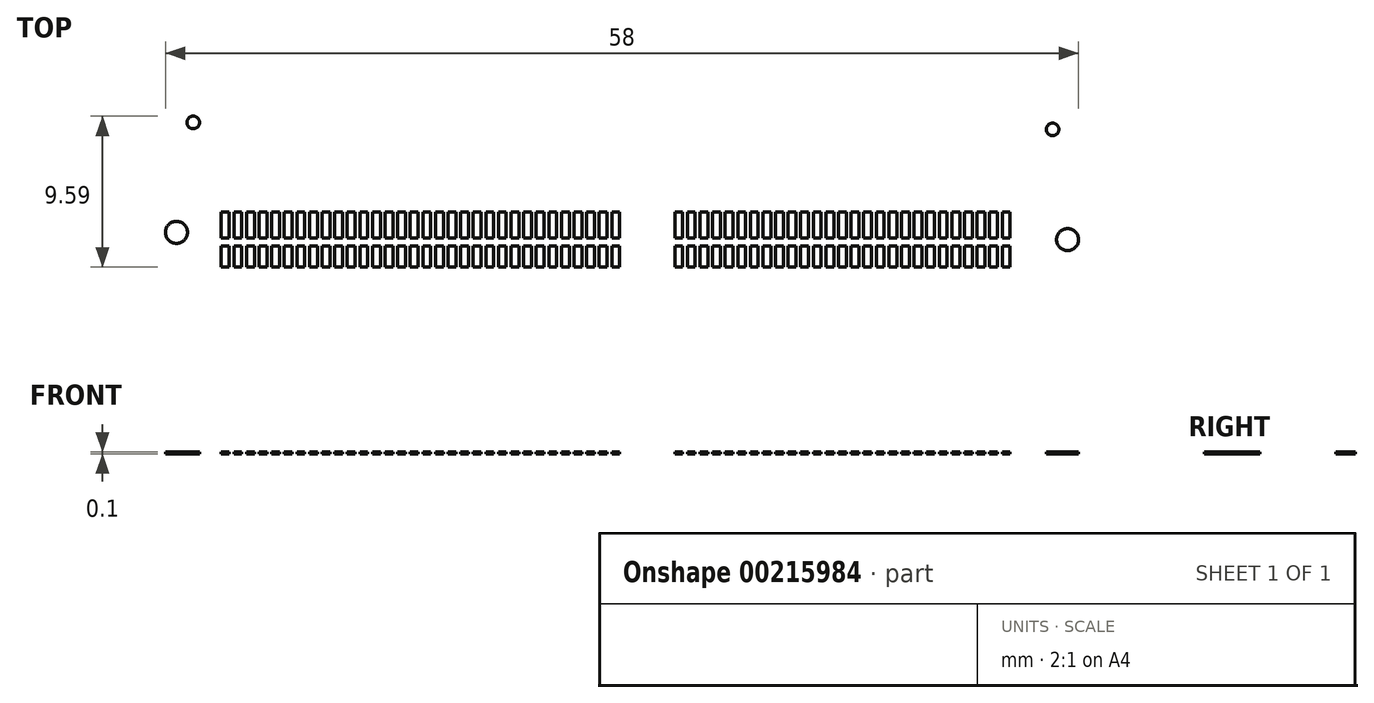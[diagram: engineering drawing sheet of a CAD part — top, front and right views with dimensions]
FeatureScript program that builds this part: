
annotation { "Feature Type Name" : "Feature", "Feature Type Description" : "" }
export const myFeature = defineFeature(function(context is Context, id is Id, definition is map)
    precondition{}
    {
        {
            var Q0;
            Q0=qCreatedBy(makeId("Top.planeOp"), FACE);
            var sketch = newSketch(context, id + "F0", { "sketchPlane" : qUnion([Q0])});
            skLineSegment(sketch, "E0.bottom", {"start": v(-25.45, 1.75) * mm, "end": v(-24.95, 1.75) * mm});
            skLineSegment(sketch, "E0.top", {"start": v(-25.45, 0.1) * mm, "end": v(-24.95, 0.1) * mm});
            skLineSegment(sketch, "E0.left", {"start": v(-25.45, 1.75) * mm, "end": v(-25.45, 0.1) * mm});
            skLineSegment(sketch, "E0.right", {"start": v(-24.95, 1.75) * mm, "end": v(-24.95, 0.1) * mm});
            skLineSegment(sketch, "E1.bottom", {"start": v(-25.45, -0.4) * mm, "end": v(-24.95, -0.4) * mm});
            skLineSegment(sketch, "E1.top", {"start": v(-25.45, -1.75) * mm, "end": v(-24.95, -1.75) * mm});
            skLineSegment(sketch, "E1.left", {"start": v(-25.45, -0.4) * mm, "end": v(-25.45, -1.75) * mm});
            skLineSegment(sketch, "E1.right", {"start": v(-24.95, -0.4) * mm, "end": v(-24.95, -1.75) * mm});
            skPoint(sketch, "E2", {"position": v(-25.2, -1.75) * mm});
            skLineSegment(sketch, "E3.1.0.0", {"start": v(-24.15, 1.75) * mm, "end": v(-24.15, 0.1) * mm});
            skLineSegment(sketch, "E3.1.0.1", {"start": v(-24.65, -0.4) * mm, "end": v(-24.65, -1.75) * mm});
            skLineSegment(sketch, "E3.1.0.2", {"start": v(-24.65, 0.1) * mm, "end": v(-24.15, 0.1) * mm});
            skLineSegment(sketch, "E3.1.0.3", {"start": v(-24.15, -0.4) * mm, "end": v(-24.15, -1.75) * mm});
            skPoint(sketch, "E3.1.0.4", {"position": v(-24.4, -1.75) * mm});
            skLineSegment(sketch, "E3.1.0.5", {"start": v(-24.65, -0.4) * mm, "end": v(-24.15, -0.4) * mm});
            skLineSegment(sketch, "E3.1.0.6", {"start": v(-24.65, 1.75) * mm, "end": v(-24.15, 1.75) * mm});
            skLineSegment(sketch, "E3.1.0.7", {"start": v(-24.65, 1.75) * mm, "end": v(-24.65, 0.1) * mm});
            skLineSegment(sketch, "E3.1.0.8", {"start": v(-24.65, -1.75) * mm, "end": v(-24.15, -1.75) * mm});
            skLineSegment(sketch, "E3.2.0.0", {"start": v(-23.35, 1.75) * mm, "end": v(-23.35, 0.1) * mm});
            skLineSegment(sketch, "E3.2.0.1", {"start": v(-23.85, -0.4) * mm, "end": v(-23.85, -1.75) * mm});
            skLineSegment(sketch, "E3.2.0.2", {"start": v(-23.85, 0.1) * mm, "end": v(-23.35, 0.1) * mm});
            skLineSegment(sketch, "E3.2.0.3", {"start": v(-23.35, -0.4) * mm, "end": v(-23.35, -1.75) * mm});
            skPoint(sketch, "E3.2.0.4", {"position": v(-23.6, -1.75) * mm});
            skLineSegment(sketch, "E3.2.0.5", {"start": v(-23.85, -0.4) * mm, "end": v(-23.35, -0.4) * mm});
            skLineSegment(sketch, "E3.2.0.6", {"start": v(-23.85, 1.75) * mm, "end": v(-23.35, 1.75) * mm});
            skLineSegment(sketch, "E3.2.0.7", {"start": v(-23.85, 1.75) * mm, "end": v(-23.85, 0.1) * mm});
            skLineSegment(sketch, "E3.2.0.8", {"start": v(-23.85, -1.75) * mm, "end": v(-23.35, -1.75) * mm});
            skLineSegment(sketch, "E3.3.0.0", {"start": v(-22.55, 1.75) * mm, "end": v(-22.55, 0.1) * mm});
            skLineSegment(sketch, "E3.3.0.1", {"start": v(-23.05, -0.4) * mm, "end": v(-23.05, -1.75) * mm});
            skLineSegment(sketch, "E3.3.0.2", {"start": v(-23.05, 0.1) * mm, "end": v(-22.55, 0.1) * mm});
            skLineSegment(sketch, "E3.3.0.3", {"start": v(-22.55, -0.4) * mm, "end": v(-22.55, -1.75) * mm});
            skPoint(sketch, "E3.3.0.4", {"position": v(-22.8, -1.75) * mm});
            skLineSegment(sketch, "E3.3.0.5", {"start": v(-23.05, -0.4) * mm, "end": v(-22.55, -0.4) * mm});
            skLineSegment(sketch, "E3.3.0.6", {"start": v(-23.05, 1.75) * mm, "end": v(-22.55, 1.75) * mm});
            skLineSegment(sketch, "E3.3.0.7", {"start": v(-23.05, 1.75) * mm, "end": v(-23.05, 0.1) * mm});
            skLineSegment(sketch, "E3.3.0.8", {"start": v(-23.05, -1.75) * mm, "end": v(-22.55, -1.75) * mm});
            skLineSegment(sketch, "E3.4.0.0", {"start": v(-21.75, 1.75) * mm, "end": v(-21.75, 0.1) * mm});
            skLineSegment(sketch, "E3.4.0.1", {"start": v(-22.25, -0.4) * mm, "end": v(-22.25, -1.75) * mm});
            skLineSegment(sketch, "E3.4.0.2", {"start": v(-22.25, 0.1) * mm, "end": v(-21.75, 0.1) * mm});
            skLineSegment(sketch, "E3.4.0.3", {"start": v(-21.75, -0.4) * mm, "end": v(-21.75, -1.75) * mm});
            skPoint(sketch, "E3.4.0.4", {"position": v(-22, -1.75) * mm});
            skLineSegment(sketch, "E3.4.0.5", {"start": v(-22.25, -0.4) * mm, "end": v(-21.75, -0.4) * mm});
            skLineSegment(sketch, "E3.4.0.6", {"start": v(-22.25, 1.75) * mm, "end": v(-21.75, 1.75) * mm});
            skLineSegment(sketch, "E3.4.0.7", {"start": v(-22.25, 1.75) * mm, "end": v(-22.25, 0.1) * mm});
            skLineSegment(sketch, "E3.4.0.8", {"start": v(-22.25, -1.75) * mm, "end": v(-21.75, -1.75) * mm});
            skLineSegment(sketch, "E3.5.0.0", {"start": v(-20.95, 1.75) * mm, "end": v(-20.95, 0.1) * mm});
            skLineSegment(sketch, "E3.5.0.1", {"start": v(-21.45, -0.4) * mm, "end": v(-21.45, -1.75) * mm});
            skLineSegment(sketch, "E3.5.0.2", {"start": v(-21.45, 0.1) * mm, "end": v(-20.95, 0.1) * mm});
            skLineSegment(sketch, "E3.5.0.3", {"start": v(-20.95, -0.4) * mm, "end": v(-20.95, -1.75) * mm});
            skPoint(sketch, "E3.5.0.4", {"position": v(-21.2, -1.75) * mm});
            skLineSegment(sketch, "E3.5.0.5", {"start": v(-21.45, -0.4) * mm, "end": v(-20.95, -0.4) * mm});
            skLineSegment(sketch, "E3.5.0.6", {"start": v(-21.45, 1.75) * mm, "end": v(-20.95, 1.75) * mm});
            skLineSegment(sketch, "E3.5.0.7", {"start": v(-21.45, 1.75) * mm, "end": v(-21.45, 0.1) * mm});
            skLineSegment(sketch, "E3.5.0.8", {"start": v(-21.45, -1.75) * mm, "end": v(-20.95, -1.75) * mm});
            skLineSegment(sketch, "E3.6.0.0", {"start": v(-20.15, 1.75) * mm, "end": v(-20.15, 0.1) * mm});
            skLineSegment(sketch, "E3.6.0.1", {"start": v(-20.65, -0.4) * mm, "end": v(-20.65, -1.75) * mm});
            skLineSegment(sketch, "E3.6.0.2", {"start": v(-20.65, 0.1) * mm, "end": v(-20.15, 0.1) * mm});
            skLineSegment(sketch, "E3.6.0.3", {"start": v(-20.15, -0.4) * mm, "end": v(-20.15, -1.75) * mm});
            skPoint(sketch, "E3.6.0.4", {"position": v(-20.4, -1.75) * mm});
            skLineSegment(sketch, "E3.6.0.5", {"start": v(-20.65, -0.4) * mm, "end": v(-20.15, -0.4) * mm});
            skLineSegment(sketch, "E3.6.0.6", {"start": v(-20.65, 1.75) * mm, "end": v(-20.15, 1.75) * mm});
            skLineSegment(sketch, "E3.6.0.7", {"start": v(-20.65, 1.75) * mm, "end": v(-20.65, 0.1) * mm});
            skLineSegment(sketch, "E3.6.0.8", {"start": v(-20.65, -1.75) * mm, "end": v(-20.15, -1.75) * mm});
            skLineSegment(sketch, "E3.7.0.0", {"start": v(-19.35, 1.75) * mm, "end": v(-19.35, 0.1) * mm});
            skLineSegment(sketch, "E3.7.0.1", {"start": v(-19.85, -0.4) * mm, "end": v(-19.85, -1.75) * mm});
            skLineSegment(sketch, "E3.7.0.2", {"start": v(-19.85, 0.1) * mm, "end": v(-19.35, 0.1) * mm});
            skLineSegment(sketch, "E3.7.0.3", {"start": v(-19.35, -0.4) * mm, "end": v(-19.35, -1.75) * mm});
            skPoint(sketch, "E3.7.0.4", {"position": v(-19.6, -1.75) * mm});
            skLineSegment(sketch, "E3.7.0.5", {"start": v(-19.85, -0.4) * mm, "end": v(-19.35, -0.4) * mm});
            skLineSegment(sketch, "E3.7.0.6", {"start": v(-19.85, 1.75) * mm, "end": v(-19.35, 1.75) * mm});
            skLineSegment(sketch, "E3.7.0.7", {"start": v(-19.85, 1.75) * mm, "end": v(-19.85, 0.1) * mm});
            skLineSegment(sketch, "E3.7.0.8", {"start": v(-19.85, -1.75) * mm, "end": v(-19.35, -1.75) * mm});
            skLineSegment(sketch, "E3.8.0.0", {"start": v(-18.55, 1.75) * mm, "end": v(-18.55, 0.1) * mm});
            skLineSegment(sketch, "E3.8.0.1", {"start": v(-19.05, -0.4) * mm, "end": v(-19.05, -1.75) * mm});
            skLineSegment(sketch, "E3.8.0.2", {"start": v(-19.05, 0.1) * mm, "end": v(-18.55, 0.1) * mm});
            skLineSegment(sketch, "E3.8.0.3", {"start": v(-18.55, -0.4) * mm, "end": v(-18.55, -1.75) * mm});
            skPoint(sketch, "E3.8.0.4", {"position": v(-18.8, -1.75) * mm});
            skLineSegment(sketch, "E3.8.0.5", {"start": v(-19.05, -0.4) * mm, "end": v(-18.55, -0.4) * mm});
            skLineSegment(sketch, "E3.8.0.6", {"start": v(-19.05, 1.75) * mm, "end": v(-18.55, 1.75) * mm});
            skLineSegment(sketch, "E3.8.0.7", {"start": v(-19.05, 1.75) * mm, "end": v(-19.05, 0.1) * mm});
            skLineSegment(sketch, "E3.8.0.8", {"start": v(-19.05, -1.75) * mm, "end": v(-18.55, -1.75) * mm});
            skLineSegment(sketch, "E3.9.0.0", {"start": v(-17.75, 1.75) * mm, "end": v(-17.75, 0.1) * mm});
            skLineSegment(sketch, "E3.9.0.1", {"start": v(-18.25, -0.4) * mm, "end": v(-18.25, -1.75) * mm});
            skLineSegment(sketch, "E3.9.0.2", {"start": v(-18.25, 0.1) * mm, "end": v(-17.75, 0.1) * mm});
            skLineSegment(sketch, "E3.9.0.3", {"start": v(-17.75, -0.4) * mm, "end": v(-17.75, -1.75) * mm});
            skPoint(sketch, "E3.9.0.4", {"position": v(-18, -1.75) * mm});
            skLineSegment(sketch, "E3.9.0.5", {"start": v(-18.25, -0.4) * mm, "end": v(-17.75, -0.4) * mm});
            skLineSegment(sketch, "E3.9.0.6", {"start": v(-18.25, 1.75) * mm, "end": v(-17.75, 1.75) * mm});
            skLineSegment(sketch, "E3.9.0.7", {"start": v(-18.25, 1.75) * mm, "end": v(-18.25, 0.1) * mm});
            skLineSegment(sketch, "E3.9.0.8", {"start": v(-18.25, -1.75) * mm, "end": v(-17.75, -1.75) * mm});
            skLineSegment(sketch, "E3.10.0.0", {"start": v(-16.95, 1.75) * mm, "end": v(-16.95, 0.1) * mm});
            skLineSegment(sketch, "E3.10.0.1", {"start": v(-17.45, -0.4) * mm, "end": v(-17.45, -1.75) * mm});
            skLineSegment(sketch, "E3.10.0.2", {"start": v(-17.45, 0.1) * mm, "end": v(-16.95, 0.1) * mm});
            skLineSegment(sketch, "E3.10.0.3", {"start": v(-16.95, -0.4) * mm, "end": v(-16.95, -1.75) * mm});
            skPoint(sketch, "E3.10.0.4", {"position": v(-17.2, -1.75) * mm});
            skLineSegment(sketch, "E3.10.0.5", {"start": v(-17.45, -0.4) * mm, "end": v(-16.95, -0.4) * mm});
            skLineSegment(sketch, "E3.10.0.6", {"start": v(-17.45, 1.75) * mm, "end": v(-16.95, 1.75) * mm});
            skLineSegment(sketch, "E3.10.0.7", {"start": v(-17.45, 1.75) * mm, "end": v(-17.45, 0.1) * mm});
            skLineSegment(sketch, "E3.10.0.8", {"start": v(-17.45, -1.75) * mm, "end": v(-16.95, -1.75) * mm});
            skLineSegment(sketch, "E3.11.0.0", {"start": v(-16.15, 1.75) * mm, "end": v(-16.15, 0.1) * mm});
            skLineSegment(sketch, "E3.11.0.1", {"start": v(-16.65, -0.4) * mm, "end": v(-16.65, -1.75) * mm});
            skLineSegment(sketch, "E3.11.0.2", {"start": v(-16.65, 0.1) * mm, "end": v(-16.15, 0.1) * mm});
            skLineSegment(sketch, "E3.11.0.3", {"start": v(-16.15, -0.4) * mm, "end": v(-16.15, -1.75) * mm});
            skPoint(sketch, "E3.11.0.4", {"position": v(-16.4, -1.75) * mm});
            skLineSegment(sketch, "E3.11.0.5", {"start": v(-16.65, -0.4) * mm, "end": v(-16.15, -0.4) * mm});
            skLineSegment(sketch, "E3.11.0.6", {"start": v(-16.65, 1.75) * mm, "end": v(-16.15, 1.75) * mm});
            skLineSegment(sketch, "E3.11.0.7", {"start": v(-16.65, 1.75) * mm, "end": v(-16.65, 0.1) * mm});
            skLineSegment(sketch, "E3.11.0.8", {"start": v(-16.65, -1.75) * mm, "end": v(-16.15, -1.75) * mm});
            skLineSegment(sketch, "E3.12.0.0", {"start": v(-15.35, 1.75) * mm, "end": v(-15.35, 0.1) * mm});
            skLineSegment(sketch, "E3.12.0.1", {"start": v(-15.85, -0.4) * mm, "end": v(-15.85, -1.75) * mm});
            skLineSegment(sketch, "E3.12.0.2", {"start": v(-15.85, 0.1) * mm, "end": v(-15.35, 0.1) * mm});
            skLineSegment(sketch, "E3.12.0.3", {"start": v(-15.35, -0.4) * mm, "end": v(-15.35, -1.75) * mm});
            skPoint(sketch, "E3.12.0.4", {"position": v(-15.6, -1.75) * mm});
            skLineSegment(sketch, "E3.12.0.5", {"start": v(-15.85, -0.4) * mm, "end": v(-15.35, -0.4) * mm});
            skLineSegment(sketch, "E3.12.0.6", {"start": v(-15.85, 1.75) * mm, "end": v(-15.35, 1.75) * mm});
            skLineSegment(sketch, "E3.12.0.7", {"start": v(-15.85, 1.75) * mm, "end": v(-15.85, 0.1) * mm});
            skLineSegment(sketch, "E3.12.0.8", {"start": v(-15.85, -1.75) * mm, "end": v(-15.35, -1.75) * mm});
            skLineSegment(sketch, "E3.13.0.0", {"start": v(-14.55, 1.75) * mm, "end": v(-14.55, 0.1) * mm});
            skLineSegment(sketch, "E3.13.0.1", {"start": v(-15.05, -0.4) * mm, "end": v(-15.05, -1.75) * mm});
            skLineSegment(sketch, "E3.13.0.2", {"start": v(-15.05, 0.1) * mm, "end": v(-14.55, 0.1) * mm});
            skLineSegment(sketch, "E3.13.0.3", {"start": v(-14.55, -0.4) * mm, "end": v(-14.55, -1.75) * mm});
            skPoint(sketch, "E3.13.0.4", {"position": v(-14.8, -1.75) * mm});
            skLineSegment(sketch, "E3.13.0.5", {"start": v(-15.05, -0.4) * mm, "end": v(-14.55, -0.4) * mm});
            skLineSegment(sketch, "E3.13.0.6", {"start": v(-15.05, 1.75) * mm, "end": v(-14.55, 1.75) * mm});
            skLineSegment(sketch, "E3.13.0.7", {"start": v(-15.05, 1.75) * mm, "end": v(-15.05, 0.1) * mm});
            skLineSegment(sketch, "E3.13.0.8", {"start": v(-15.05, -1.75) * mm, "end": v(-14.55, -1.75) * mm});
            skLineSegment(sketch, "E3.14.0.0", {"start": v(-13.75, 1.75) * mm, "end": v(-13.75, 0.1) * mm});
            skLineSegment(sketch, "E3.14.0.1", {"start": v(-14.25, -0.4) * mm, "end": v(-14.25, -1.75) * mm});
            skLineSegment(sketch, "E3.14.0.2", {"start": v(-14.25, 0.1) * mm, "end": v(-13.75, 0.1) * mm});
            skLineSegment(sketch, "E3.14.0.3", {"start": v(-13.75, -0.4) * mm, "end": v(-13.75, -1.75) * mm});
            skPoint(sketch, "E3.14.0.4", {"position": v(-14, -1.75) * mm});
            skLineSegment(sketch, "E3.14.0.5", {"start": v(-14.25, -0.4) * mm, "end": v(-13.75, -0.4) * mm});
            skLineSegment(sketch, "E3.14.0.6", {"start": v(-14.25, 1.75) * mm, "end": v(-13.75, 1.75) * mm});
            skLineSegment(sketch, "E3.14.0.7", {"start": v(-14.25, 1.75) * mm, "end": v(-14.25, 0.1) * mm});
            skLineSegment(sketch, "E3.14.0.8", {"start": v(-14.25, -1.75) * mm, "end": v(-13.75, -1.75) * mm});
            skLineSegment(sketch, "E3.15.0.0", {"start": v(-12.95, 1.75) * mm, "end": v(-12.95, 0.1) * mm});
            skLineSegment(sketch, "E3.15.0.1", {"start": v(-13.45, -0.4) * mm, "end": v(-13.45, -1.75) * mm});
            skLineSegment(sketch, "E3.15.0.2", {"start": v(-13.45, 0.1) * mm, "end": v(-12.95, 0.1) * mm});
            skLineSegment(sketch, "E3.15.0.3", {"start": v(-12.95, -0.4) * mm, "end": v(-12.95, -1.75) * mm});
            skPoint(sketch, "E3.15.0.4", {"position": v(-13.2, -1.75) * mm});
            skLineSegment(sketch, "E3.15.0.5", {"start": v(-13.45, -0.4) * mm, "end": v(-12.95, -0.4) * mm});
            skLineSegment(sketch, "E3.15.0.6", {"start": v(-13.45, 1.75) * mm, "end": v(-12.95, 1.75) * mm});
            skLineSegment(sketch, "E3.15.0.7", {"start": v(-13.45, 1.75) * mm, "end": v(-13.45, 0.1) * mm});
            skLineSegment(sketch, "E3.15.0.8", {"start": v(-13.45, -1.75) * mm, "end": v(-12.95, -1.75) * mm});
            skLineSegment(sketch, "E3.16.0.0", {"start": v(-12.15, 1.75) * mm, "end": v(-12.15, 0.1) * mm});
            skLineSegment(sketch, "E3.16.0.1", {"start": v(-12.65, -0.4) * mm, "end": v(-12.65, -1.75) * mm});
            skLineSegment(sketch, "E3.16.0.2", {"start": v(-12.65, 0.1) * mm, "end": v(-12.15, 0.1) * mm});
            skLineSegment(sketch, "E3.16.0.3", {"start": v(-12.15, -0.4) * mm, "end": v(-12.15, -1.75) * mm});
            skPoint(sketch, "E3.16.0.4", {"position": v(-12.4, -1.75) * mm});
            skLineSegment(sketch, "E3.16.0.5", {"start": v(-12.65, -0.4) * mm, "end": v(-12.15, -0.4) * mm});
            skLineSegment(sketch, "E3.16.0.6", {"start": v(-12.65, 1.75) * mm, "end": v(-12.15, 1.75) * mm});
            skLineSegment(sketch, "E3.16.0.7", {"start": v(-12.65, 1.75) * mm, "end": v(-12.65, 0.1) * mm});
            skLineSegment(sketch, "E3.16.0.8", {"start": v(-12.65, -1.75) * mm, "end": v(-12.15, -1.75) * mm});
            skLineSegment(sketch, "E3.17.0.0", {"start": v(-11.35, 1.75) * mm, "end": v(-11.35, 0.1) * mm});
            skLineSegment(sketch, "E3.17.0.1", {"start": v(-11.85, -0.4) * mm, "end": v(-11.85, -1.75) * mm});
            skLineSegment(sketch, "E3.17.0.2", {"start": v(-11.85, 0.1) * mm, "end": v(-11.35, 0.1) * mm});
            skLineSegment(sketch, "E3.17.0.3", {"start": v(-11.35, -0.4) * mm, "end": v(-11.35, -1.75) * mm});
            skPoint(sketch, "E3.17.0.4", {"position": v(-11.6, -1.75) * mm});
            skLineSegment(sketch, "E3.17.0.5", {"start": v(-11.85, -0.4) * mm, "end": v(-11.35, -0.4) * mm});
            skLineSegment(sketch, "E3.17.0.6", {"start": v(-11.85, 1.75) * mm, "end": v(-11.35, 1.75) * mm});
            skLineSegment(sketch, "E3.17.0.7", {"start": v(-11.85, 1.75) * mm, "end": v(-11.85, 0.1) * mm});
            skLineSegment(sketch, "E3.17.0.8", {"start": v(-11.85, -1.75) * mm, "end": v(-11.35, -1.75) * mm});
            skLineSegment(sketch, "E3.18.0.0", {"start": v(-10.55, 1.75) * mm, "end": v(-10.55, 0.1) * mm});
            skLineSegment(sketch, "E3.18.0.1", {"start": v(-11.05, -0.4) * mm, "end": v(-11.05, -1.75) * mm});
            skLineSegment(sketch, "E3.18.0.2", {"start": v(-11.05, 0.1) * mm, "end": v(-10.55, 0.1) * mm});
            skLineSegment(sketch, "E3.18.0.3", {"start": v(-10.55, -0.4) * mm, "end": v(-10.55, -1.75) * mm});
            skPoint(sketch, "E3.18.0.4", {"position": v(-10.8, -1.75) * mm});
            skLineSegment(sketch, "E3.18.0.5", {"start": v(-11.05, -0.4) * mm, "end": v(-10.55, -0.4) * mm});
            skLineSegment(sketch, "E3.18.0.6", {"start": v(-11.05, 1.75) * mm, "end": v(-10.55, 1.75) * mm});
            skLineSegment(sketch, "E3.18.0.7", {"start": v(-11.05, 1.75) * mm, "end": v(-11.05, 0.1) * mm});
            skLineSegment(sketch, "E3.18.0.8", {"start": v(-11.05, -1.75) * mm, "end": v(-10.55, -1.75) * mm});
            skLineSegment(sketch, "E3.19.0.0", {"start": v(-9.75, 1.75) * mm, "end": v(-9.75, 0.1) * mm});
            skLineSegment(sketch, "E3.19.0.1", {"start": v(-10.25, -0.4) * mm, "end": v(-10.25, -1.75) * mm});
            skLineSegment(sketch, "E3.19.0.2", {"start": v(-10.25, 0.1) * mm, "end": v(-9.75, 0.1) * mm});
            skLineSegment(sketch, "E3.19.0.3", {"start": v(-9.75, -0.4) * mm, "end": v(-9.75, -1.75) * mm});
            skPoint(sketch, "E3.19.0.4", {"position": v(-10, -1.75) * mm});
            skLineSegment(sketch, "E3.19.0.5", {"start": v(-10.25, -0.4) * mm, "end": v(-9.75, -0.4) * mm});
            skLineSegment(sketch, "E3.19.0.6", {"start": v(-10.25, 1.75) * mm, "end": v(-9.75, 1.75) * mm});
            skLineSegment(sketch, "E3.19.0.7", {"start": v(-10.25, 1.75) * mm, "end": v(-10.25, 0.1) * mm});
            skLineSegment(sketch, "E3.19.0.8", {"start": v(-10.25, -1.75) * mm, "end": v(-9.75, -1.75) * mm});
            skLineSegment(sketch, "E3.20.0.0", {"start": v(-8.95, 1.75) * mm, "end": v(-8.95, 0.1) * mm});
            skLineSegment(sketch, "E3.20.0.1", {"start": v(-9.45, -0.4) * mm, "end": v(-9.45, -1.75) * mm});
            skLineSegment(sketch, "E3.20.0.2", {"start": v(-9.45, 0.1) * mm, "end": v(-8.95, 0.1) * mm});
            skLineSegment(sketch, "E3.20.0.3", {"start": v(-8.95, -0.4) * mm, "end": v(-8.95, -1.75) * mm});
            skPoint(sketch, "E3.20.0.4", {"position": v(-9.2, -1.75) * mm});
            skLineSegment(sketch, "E3.20.0.5", {"start": v(-9.45, -0.4) * mm, "end": v(-8.95, -0.4) * mm});
            skLineSegment(sketch, "E3.20.0.6", {"start": v(-9.45, 1.75) * mm, "end": v(-8.95, 1.75) * mm});
            skLineSegment(sketch, "E3.20.0.7", {"start": v(-9.45, 1.75) * mm, "end": v(-9.45, 0.1) * mm});
            skLineSegment(sketch, "E3.20.0.8", {"start": v(-9.45, -1.75) * mm, "end": v(-8.95, -1.75) * mm});
            skLineSegment(sketch, "E3.21.0.0", {"start": v(-8.15, 1.75) * mm, "end": v(-8.15, 0.1) * mm});
            skLineSegment(sketch, "E3.21.0.1", {"start": v(-8.65, -0.4) * mm, "end": v(-8.65, -1.75) * mm});
            skLineSegment(sketch, "E3.21.0.2", {"start": v(-8.65, 0.1) * mm, "end": v(-8.15, 0.1) * mm});
            skLineSegment(sketch, "E3.21.0.3", {"start": v(-8.15, -0.4) * mm, "end": v(-8.15, -1.75) * mm});
            skPoint(sketch, "E3.21.0.4", {"position": v(-8.4, -1.75) * mm});
            skLineSegment(sketch, "E3.21.0.5", {"start": v(-8.65, -0.4) * mm, "end": v(-8.15, -0.4) * mm});
            skLineSegment(sketch, "E3.21.0.6", {"start": v(-8.65, 1.75) * mm, "end": v(-8.15, 1.75) * mm});
            skLineSegment(sketch, "E3.21.0.7", {"start": v(-8.65, 1.75) * mm, "end": v(-8.65, 0.1) * mm});
            skLineSegment(sketch, "E3.21.0.8", {"start": v(-8.65, -1.75) * mm, "end": v(-8.15, -1.75) * mm});
            skLineSegment(sketch, "E3.22.0.0", {"start": v(-7.35, 1.75) * mm, "end": v(-7.35, 0.1) * mm});
            skLineSegment(sketch, "E3.22.0.1", {"start": v(-7.85, -0.4) * mm, "end": v(-7.85, -1.75) * mm});
            skLineSegment(sketch, "E3.22.0.2", {"start": v(-7.85, 0.1) * mm, "end": v(-7.35, 0.1) * mm});
            skLineSegment(sketch, "E3.22.0.3", {"start": v(-7.35, -0.4) * mm, "end": v(-7.35, -1.75) * mm});
            skPoint(sketch, "E3.22.0.4", {"position": v(-7.6, -1.75) * mm});
            skLineSegment(sketch, "E3.22.0.5", {"start": v(-7.85, -0.4) * mm, "end": v(-7.35, -0.4) * mm});
            skLineSegment(sketch, "E3.22.0.6", {"start": v(-7.85, 1.75) * mm, "end": v(-7.35, 1.75) * mm});
            skLineSegment(sketch, "E3.22.0.7", {"start": v(-7.85, 1.75) * mm, "end": v(-7.85, 0.1) * mm});
            skLineSegment(sketch, "E3.22.0.8", {"start": v(-7.85, -1.75) * mm, "end": v(-7.35, -1.75) * mm});
            skLineSegment(sketch, "E3.23.0.0", {"start": v(-6.55, 1.75) * mm, "end": v(-6.55, 0.1) * mm});
            skLineSegment(sketch, "E3.23.0.1", {"start": v(-7.05, -0.4) * mm, "end": v(-7.05, -1.75) * mm});
            skLineSegment(sketch, "E3.23.0.2", {"start": v(-7.05, 0.1) * mm, "end": v(-6.55, 0.1) * mm});
            skLineSegment(sketch, "E3.23.0.3", {"start": v(-6.55, -0.4) * mm, "end": v(-6.55, -1.75) * mm});
            skPoint(sketch, "E3.23.0.4", {"position": v(-6.8, -1.75) * mm});
            skLineSegment(sketch, "E3.23.0.5", {"start": v(-7.05, -0.4) * mm, "end": v(-6.55, -0.4) * mm});
            skLineSegment(sketch, "E3.23.0.6", {"start": v(-7.05, 1.75) * mm, "end": v(-6.55, 1.75) * mm});
            skLineSegment(sketch, "E3.23.0.7", {"start": v(-7.05, 1.75) * mm, "end": v(-7.05, 0.1) * mm});
            skLineSegment(sketch, "E3.23.0.8", {"start": v(-7.05, -1.75) * mm, "end": v(-6.55, -1.75) * mm});
            skLineSegment(sketch, "E3.24.0.0", {"start": v(-5.75, 1.75) * mm, "end": v(-5.75, 0.1) * mm});
            skLineSegment(sketch, "E3.24.0.1", {"start": v(-6.25, -0.4) * mm, "end": v(-6.25, -1.75) * mm});
            skLineSegment(sketch, "E3.24.0.2", {"start": v(-6.25, 0.1) * mm, "end": v(-5.75, 0.1) * mm});
            skLineSegment(sketch, "E3.24.0.3", {"start": v(-5.75, -0.4) * mm, "end": v(-5.75, -1.75) * mm});
            skPoint(sketch, "E3.24.0.4", {"position": v(-6, -1.75) * mm});
            skLineSegment(sketch, "E3.24.0.5", {"start": v(-6.25, -0.4) * mm, "end": v(-5.75, -0.4) * mm});
            skLineSegment(sketch, "E3.24.0.6", {"start": v(-6.25, 1.75) * mm, "end": v(-5.75, 1.75) * mm});
            skLineSegment(sketch, "E3.24.0.7", {"start": v(-6.25, 1.75) * mm, "end": v(-6.25, 0.1) * mm});
            skLineSegment(sketch, "E3.24.0.8", {"start": v(-6.25, -1.75) * mm, "end": v(-5.75, -1.75) * mm});
            skLineSegment(sketch, "E3.25.0.0", {"start": v(-4.95, 1.75) * mm, "end": v(-4.95, 0.1) * mm});
            skLineSegment(sketch, "E3.25.0.1", {"start": v(-5.45, -0.4) * mm, "end": v(-5.45, -1.75) * mm});
            skLineSegment(sketch, "E3.25.0.2", {"start": v(-5.45, 0.1) * mm, "end": v(-4.95, 0.1) * mm});
            skLineSegment(sketch, "E3.25.0.3", {"start": v(-4.95, -0.4) * mm, "end": v(-4.95, -1.75) * mm});
            skPoint(sketch, "E3.25.0.4", {"position": v(-5.2, -1.75) * mm});
            skLineSegment(sketch, "E3.25.0.5", {"start": v(-5.45, -0.4) * mm, "end": v(-4.95, -0.4) * mm});
            skLineSegment(sketch, "E3.25.0.6", {"start": v(-5.45, 1.75) * mm, "end": v(-4.95, 1.75) * mm});
            skLineSegment(sketch, "E3.25.0.7", {"start": v(-5.45, 1.75) * mm, "end": v(-5.45, 0.1) * mm});
            skLineSegment(sketch, "E3.25.0.8", {"start": v(-5.45, -1.75) * mm, "end": v(-4.95, -1.75) * mm});
            skLineSegment(sketch, "E3.26.0.0", {"start": v(-4.15, 1.75) * mm, "end": v(-4.15, 0.1) * mm});
            skLineSegment(sketch, "E3.26.0.1", {"start": v(-4.65, -0.4) * mm, "end": v(-4.65, -1.75) * mm});
            skLineSegment(sketch, "E3.26.0.2", {"start": v(-4.65, 0.1) * mm, "end": v(-4.15, 0.1) * mm});
            skLineSegment(sketch, "E3.26.0.3", {"start": v(-4.15, -0.4) * mm, "end": v(-4.15, -1.75) * mm});
            skPoint(sketch, "E3.26.0.4", {"position": v(-4.4, -1.75) * mm});
            skLineSegment(sketch, "E3.26.0.5", {"start": v(-4.65, -0.4) * mm, "end": v(-4.15, -0.4) * mm});
            skLineSegment(sketch, "E3.26.0.6", {"start": v(-4.65, 1.75) * mm, "end": v(-4.15, 1.75) * mm});
            skLineSegment(sketch, "E3.26.0.7", {"start": v(-4.65, 1.75) * mm, "end": v(-4.65, 0.1) * mm});
            skLineSegment(sketch, "E3.26.0.8", {"start": v(-4.65, -1.75) * mm, "end": v(-4.15, -1.75) * mm});
            skLineSegment(sketch, "E3.27.0.0", {"start": v(-3.35, 1.75) * mm, "end": v(-3.35, 0.1) * mm});
            skLineSegment(sketch, "E3.27.0.1", {"start": v(-3.85, -0.4) * mm, "end": v(-3.85, -1.75) * mm});
            skLineSegment(sketch, "E3.27.0.2", {"start": v(-3.85, 0.1) * mm, "end": v(-3.35, 0.1) * mm});
            skLineSegment(sketch, "E3.27.0.3", {"start": v(-3.35, -0.4) * mm, "end": v(-3.35, -1.75) * mm});
            skPoint(sketch, "E3.27.0.4", {"position": v(-3.6, -1.75) * mm});
            skLineSegment(sketch, "E3.27.0.5", {"start": v(-3.85, -0.4) * mm, "end": v(-3.35, -0.4) * mm});
            skLineSegment(sketch, "E3.27.0.6", {"start": v(-3.85, 1.75) * mm, "end": v(-3.35, 1.75) * mm});
            skLineSegment(sketch, "E3.27.0.7", {"start": v(-3.85, 1.75) * mm, "end": v(-3.85, 0.1) * mm});
            skLineSegment(sketch, "E3.27.0.8", {"start": v(-3.85, -1.75) * mm, "end": v(-3.35, -1.75) * mm});
            skLineSegment(sketch, "E3.28.0.0", {"start": v(-2.55, 1.75) * mm, "end": v(-2.55, 0.1) * mm});
            skLineSegment(sketch, "E3.28.0.1", {"start": v(-3.05, -0.4) * mm, "end": v(-3.05, -1.75) * mm});
            skLineSegment(sketch, "E3.28.0.2", {"start": v(-3.05, 0.1) * mm, "end": v(-2.55, 0.1) * mm});
            skLineSegment(sketch, "E3.28.0.3", {"start": v(-2.55, -0.4) * mm, "end": v(-2.55, -1.75) * mm});
            skPoint(sketch, "E3.28.0.4", {"position": v(-2.8, -1.75) * mm});
            skLineSegment(sketch, "E3.28.0.5", {"start": v(-3.05, -0.4) * mm, "end": v(-2.55, -0.4) * mm});
            skLineSegment(sketch, "E3.28.0.6", {"start": v(-3.05, 1.75) * mm, "end": v(-2.55, 1.75) * mm});
            skLineSegment(sketch, "E3.28.0.7", {"start": v(-3.05, 1.75) * mm, "end": v(-3.05, 0.1) * mm});
            skLineSegment(sketch, "E3.28.0.8", {"start": v(-3.05, -1.75) * mm, "end": v(-2.55, -1.75) * mm});
            skLineSegment(sketch, "E3.29.0.0", {"start": v(-1.75, 1.75) * mm, "end": v(-1.75, 0.1) * mm});
            skLineSegment(sketch, "E3.29.0.1", {"start": v(-2.25, -0.4) * mm, "end": v(-2.25, -1.75) * mm});
            skLineSegment(sketch, "E3.29.0.2", {"start": v(-2.25, 0.1) * mm, "end": v(-1.75, 0.1) * mm});
            skLineSegment(sketch, "E3.29.0.3", {"start": v(-1.75, -0.4) * mm, "end": v(-1.75, -1.75) * mm});
            skPoint(sketch, "E3.29.0.4", {"position": v(-2, -1.75) * mm});
            skLineSegment(sketch, "E3.29.0.5", {"start": v(-2.25, -0.4) * mm, "end": v(-1.75, -0.4) * mm});
            skLineSegment(sketch, "E3.29.0.6", {"start": v(-2.25, 1.75) * mm, "end": v(-1.75, 1.75) * mm});
            skLineSegment(sketch, "E3.29.0.7", {"start": v(-2.25, 1.75) * mm, "end": v(-2.25, 0.1) * mm});
            skLineSegment(sketch, "E3.29.0.8", {"start": v(-2.25, -1.75) * mm, "end": v(-1.75, -1.75) * mm});
            skLineSegment(sketch, "E3.30.0.0", {"start": v(-0.95, 1.75) * mm, "end": v(-0.95, 0.1) * mm});
            skLineSegment(sketch, "E3.30.0.1", {"start": v(-1.45, -0.4) * mm, "end": v(-1.45, -1.75) * mm});
            skLineSegment(sketch, "E3.30.0.2", {"start": v(-1.45, 0.1) * mm, "end": v(-0.95, 0.1) * mm});
            skLineSegment(sketch, "E3.30.0.3", {"start": v(-0.95, -0.4) * mm, "end": v(-0.95, -1.75) * mm});
            skPoint(sketch, "E3.30.0.4", {"position": v(-1.2, -1.75) * mm});
            skLineSegment(sketch, "E3.30.0.5", {"start": v(-1.45, -0.4) * mm, "end": v(-0.95, -0.4) * mm});
            skLineSegment(sketch, "E3.30.0.6", {"start": v(-1.45, 1.75) * mm, "end": v(-0.95, 1.75) * mm});
            skLineSegment(sketch, "E3.30.0.7", {"start": v(-1.45, 1.75) * mm, "end": v(-1.45, 0.1) * mm});
            skLineSegment(sketch, "E3.30.0.8", {"start": v(-1.45, -1.75) * mm, "end": v(-0.95, -1.75) * mm});
            skLineSegment(sketch, "E3.direction1", {"start": v(-25.45, -1.75) * mm, "end": v(-24.65, -1.75) * mm, "construction": true});
            skLineSegment(sketch, "E4.1.0.0", {"start": v(2.55, 0.1) * mm, "end": v(3.05, 0.1) * mm, "construction": true});
            skLineSegment(sketch, "E4.1.0.1", {"start": v(3.05, -0.4) * mm, "end": v(3.05, -1.75) * mm, "construction": true});
            skLineSegment(sketch, "E4.1.0.2", {"start": v(2.55, 1.75) * mm, "end": v(2.55, 0.1) * mm, "construction": true});
            skLineSegment(sketch, "E4.1.0.3", {"start": v(3.05, 1.75) * mm, "end": v(3.05, 0.1) * mm, "construction": true});
            skLineSegment(sketch, "E4.1.0.4", {"start": v(2.55, -0.4) * mm, "end": v(3.05, -0.4) * mm, "construction": true});
            skPoint(sketch, "E4.1.0.5", {"position": v(2.8, -1.75) * mm});
            skLineSegment(sketch, "E4.1.0.6", {"start": v(2.55, -0.4) * mm, "end": v(2.55, -1.75) * mm, "construction": true});
            skLineSegment(sketch, "E4.1.0.7", {"start": v(2.55, 1.75) * mm, "end": v(3.05, 1.75) * mm, "construction": true});
            skLineSegment(sketch, "E4.1.0.8", {"start": v(2.55, -1.75) * mm, "end": v(3.05, -1.75) * mm, "construction": true});
            skLineSegment(sketch, "E4.direction1", {"start": v(-1.45, -1.75) * mm, "end": v(2.55, -1.75) * mm, "construction": true});
            skLineSegment(sketch, "E5.1.0.0", {"start": v(3.85, -0.4) * mm, "end": v(3.85, -1.75) * mm});
            skLineSegment(sketch, "E5.1.0.1", {"start": v(3.85, 1.75) * mm, "end": v(3.85, 0.1) * mm});
            skPoint(sketch, "E5.1.0.2", {"position": v(3.6, -1.75) * mm});
            skLineSegment(sketch, "E5.1.0.3", {"start": v(3.35, 1.75) * mm, "end": v(3.35, 0.1) * mm});
            skLineSegment(sketch, "E5.1.0.4", {"start": v(3.35, -0.4) * mm, "end": v(3.35, -1.75) * mm});
            skLineSegment(sketch, "E5.1.0.5", {"start": v(3.35, 0.1) * mm, "end": v(3.85, 0.1) * mm});
            skLineSegment(sketch, "E5.1.0.6", {"start": v(3.35, 1.75) * mm, "end": v(3.85, 1.75) * mm});
            skLineSegment(sketch, "E5.1.0.7", {"start": v(3.35, -0.4) * mm, "end": v(3.85, -0.4) * mm});
            skLineSegment(sketch, "E5.1.0.8", {"start": v(3.35, -1.75) * mm, "end": v(3.85, -1.75) * mm});
            skLineSegment(sketch, "E5.2.0.0", {"start": v(4.65, -0.4) * mm, "end": v(4.65, -1.75) * mm});
            skLineSegment(sketch, "E5.2.0.1", {"start": v(4.65, 1.75) * mm, "end": v(4.65, 0.1) * mm});
            skPoint(sketch, "E5.2.0.2", {"position": v(4.4, -1.75) * mm});
            skLineSegment(sketch, "E5.2.0.3", {"start": v(4.15, 1.75) * mm, "end": v(4.15, 0.1) * mm});
            skLineSegment(sketch, "E5.2.0.4", {"start": v(4.15, -0.4) * mm, "end": v(4.15, -1.75) * mm});
            skLineSegment(sketch, "E5.2.0.5", {"start": v(4.15, 0.1) * mm, "end": v(4.65, 0.1) * mm});
            skLineSegment(sketch, "E5.2.0.6", {"start": v(4.15, 1.75) * mm, "end": v(4.65, 1.75) * mm});
            skLineSegment(sketch, "E5.2.0.7", {"start": v(4.15, -0.4) * mm, "end": v(4.65, -0.4) * mm});
            skLineSegment(sketch, "E5.2.0.8", {"start": v(4.15, -1.75) * mm, "end": v(4.65, -1.75) * mm});
            skLineSegment(sketch, "E5.3.0.0", {"start": v(5.45, -0.4) * mm, "end": v(5.45, -1.75) * mm});
            skLineSegment(sketch, "E5.3.0.1", {"start": v(5.45, 1.75) * mm, "end": v(5.45, 0.1) * mm});
            skPoint(sketch, "E5.3.0.2", {"position": v(5.2, -1.75) * mm});
            skLineSegment(sketch, "E5.3.0.3", {"start": v(4.95, 1.75) * mm, "end": v(4.95, 0.1) * mm});
            skLineSegment(sketch, "E5.3.0.4", {"start": v(4.95, -0.4) * mm, "end": v(4.95, -1.75) * mm});
            skLineSegment(sketch, "E5.3.0.5", {"start": v(4.95, 0.1) * mm, "end": v(5.45, 0.1) * mm});
            skLineSegment(sketch, "E5.3.0.6", {"start": v(4.95, 1.75) * mm, "end": v(5.45, 1.75) * mm});
            skLineSegment(sketch, "E5.3.0.7", {"start": v(4.95, -0.4) * mm, "end": v(5.45, -0.4) * mm});
            skLineSegment(sketch, "E5.3.0.8", {"start": v(4.95, -1.75) * mm, "end": v(5.45, -1.75) * mm});
            skLineSegment(sketch, "E5.4.0.0", {"start": v(6.25, -0.4) * mm, "end": v(6.25, -1.75) * mm});
            skLineSegment(sketch, "E5.4.0.1", {"start": v(6.25, 1.75) * mm, "end": v(6.25, 0.1) * mm});
            skPoint(sketch, "E5.4.0.2", {"position": v(6, -1.75) * mm});
            skLineSegment(sketch, "E5.4.0.3", {"start": v(5.75, 1.75) * mm, "end": v(5.75, 0.1) * mm});
            skLineSegment(sketch, "E5.4.0.4", {"start": v(5.75, -0.4) * mm, "end": v(5.75, -1.75) * mm});
            skLineSegment(sketch, "E5.4.0.5", {"start": v(5.75, 0.1) * mm, "end": v(6.25, 0.1) * mm});
            skLineSegment(sketch, "E5.4.0.6", {"start": v(5.75, 1.75) * mm, "end": v(6.25, 1.75) * mm});
            skLineSegment(sketch, "E5.4.0.7", {"start": v(5.75, -0.4) * mm, "end": v(6.25, -0.4) * mm});
            skLineSegment(sketch, "E5.4.0.8", {"start": v(5.75, -1.75) * mm, "end": v(6.25, -1.75) * mm});
            skLineSegment(sketch, "E5.5.0.0", {"start": v(7.05, -0.4) * mm, "end": v(7.05, -1.75) * mm});
            skLineSegment(sketch, "E5.5.0.1", {"start": v(7.05, 1.75) * mm, "end": v(7.05, 0.1) * mm});
            skPoint(sketch, "E5.5.0.2", {"position": v(6.8, -1.75) * mm});
            skLineSegment(sketch, "E5.5.0.3", {"start": v(6.55, 1.75) * mm, "end": v(6.55, 0.1) * mm});
            skLineSegment(sketch, "E5.5.0.4", {"start": v(6.55, -0.4) * mm, "end": v(6.55, -1.75) * mm});
            skLineSegment(sketch, "E5.5.0.5", {"start": v(6.55, 0.1) * mm, "end": v(7.05, 0.1) * mm});
            skLineSegment(sketch, "E5.5.0.6", {"start": v(6.55, 1.75) * mm, "end": v(7.05, 1.75) * mm});
            skLineSegment(sketch, "E5.5.0.7", {"start": v(6.55, -0.4) * mm, "end": v(7.05, -0.4) * mm});
            skLineSegment(sketch, "E5.5.0.8", {"start": v(6.55, -1.75) * mm, "end": v(7.05, -1.75) * mm});
            skLineSegment(sketch, "E5.6.0.0", {"start": v(7.85, -0.4) * mm, "end": v(7.85, -1.75) * mm});
            skLineSegment(sketch, "E5.6.0.1", {"start": v(7.85, 1.75) * mm, "end": v(7.85, 0.1) * mm});
            skPoint(sketch, "E5.6.0.2", {"position": v(7.6, -1.75) * mm});
            skLineSegment(sketch, "E5.6.0.3", {"start": v(7.35, 1.75) * mm, "end": v(7.35, 0.1) * mm});
            skLineSegment(sketch, "E5.6.0.4", {"start": v(7.35, -0.4) * mm, "end": v(7.35, -1.75) * mm});
            skLineSegment(sketch, "E5.6.0.5", {"start": v(7.35, 0.1) * mm, "end": v(7.85, 0.1) * mm});
            skLineSegment(sketch, "E5.6.0.6", {"start": v(7.35, 1.75) * mm, "end": v(7.85, 1.75) * mm});
            skLineSegment(sketch, "E5.6.0.7", {"start": v(7.35, -0.4) * mm, "end": v(7.85, -0.4) * mm});
            skLineSegment(sketch, "E5.6.0.8", {"start": v(7.35, -1.75) * mm, "end": v(7.85, -1.75) * mm});
            skLineSegment(sketch, "E5.7.0.0", {"start": v(8.65, -0.4) * mm, "end": v(8.65, -1.75) * mm});
            skLineSegment(sketch, "E5.7.0.1", {"start": v(8.65, 1.75) * mm, "end": v(8.65, 0.1) * mm});
            skPoint(sketch, "E5.7.0.2", {"position": v(8.4, -1.75) * mm});
            skLineSegment(sketch, "E5.7.0.3", {"start": v(8.15, 1.75) * mm, "end": v(8.15, 0.1) * mm});
            skLineSegment(sketch, "E5.7.0.4", {"start": v(8.15, -0.4) * mm, "end": v(8.15, -1.75) * mm});
            skLineSegment(sketch, "E5.7.0.5", {"start": v(8.15, 0.1) * mm, "end": v(8.65, 0.1) * mm});
            skLineSegment(sketch, "E5.7.0.6", {"start": v(8.15, 1.75) * mm, "end": v(8.65, 1.75) * mm});
            skLineSegment(sketch, "E5.7.0.7", {"start": v(8.15, -0.4) * mm, "end": v(8.65, -0.4) * mm});
            skLineSegment(sketch, "E5.7.0.8", {"start": v(8.15, -1.75) * mm, "end": v(8.65, -1.75) * mm});
            skLineSegment(sketch, "E5.8.0.0", {"start": v(9.45, -0.4) * mm, "end": v(9.45, -1.75) * mm});
            skLineSegment(sketch, "E5.8.0.1", {"start": v(9.45, 1.75) * mm, "end": v(9.45, 0.1) * mm});
            skPoint(sketch, "E5.8.0.2", {"position": v(9.2, -1.75) * mm});
            skLineSegment(sketch, "E5.8.0.3", {"start": v(8.95, 1.75) * mm, "end": v(8.95, 0.1) * mm});
            skLineSegment(sketch, "E5.8.0.4", {"start": v(8.95, -0.4) * mm, "end": v(8.95, -1.75) * mm});
            skLineSegment(sketch, "E5.8.0.5", {"start": v(8.95, 0.1) * mm, "end": v(9.45, 0.1) * mm});
            skLineSegment(sketch, "E5.8.0.6", {"start": v(8.95, 1.75) * mm, "end": v(9.45, 1.75) * mm});
            skLineSegment(sketch, "E5.8.0.7", {"start": v(8.95, -0.4) * mm, "end": v(9.45, -0.4) * mm});
            skLineSegment(sketch, "E5.8.0.8", {"start": v(8.95, -1.75) * mm, "end": v(9.45, -1.75) * mm});
            skLineSegment(sketch, "E5.9.0.0", {"start": v(10.25, -0.4) * mm, "end": v(10.25, -1.75) * mm});
            skLineSegment(sketch, "E5.9.0.1", {"start": v(10.25, 1.75) * mm, "end": v(10.25, 0.1) * mm});
            skPoint(sketch, "E5.9.0.2", {"position": v(10, -1.75) * mm});
            skLineSegment(sketch, "E5.9.0.3", {"start": v(9.75, 1.75) * mm, "end": v(9.75, 0.1) * mm});
            skLineSegment(sketch, "E5.9.0.4", {"start": v(9.75, -0.4) * mm, "end": v(9.75, -1.75) * mm});
            skLineSegment(sketch, "E5.9.0.5", {"start": v(9.75, 0.1) * mm, "end": v(10.25, 0.1) * mm});
            skLineSegment(sketch, "E5.9.0.6", {"start": v(9.75, 1.75) * mm, "end": v(10.25, 1.75) * mm});
            skLineSegment(sketch, "E5.9.0.7", {"start": v(9.75, -0.4) * mm, "end": v(10.25, -0.4) * mm});
            skLineSegment(sketch, "E5.9.0.8", {"start": v(9.75, -1.75) * mm, "end": v(10.25, -1.75) * mm});
            skLineSegment(sketch, "E5.10.0.0", {"start": v(11.05, -0.4) * mm, "end": v(11.05, -1.75) * mm});
            skLineSegment(sketch, "E5.10.0.1", {"start": v(11.05, 1.75) * mm, "end": v(11.05, 0.1) * mm});
            skPoint(sketch, "E5.10.0.2", {"position": v(10.8, -1.75) * mm});
            skLineSegment(sketch, "E5.10.0.3", {"start": v(10.55, 1.75) * mm, "end": v(10.55, 0.1) * mm});
            skLineSegment(sketch, "E5.10.0.4", {"start": v(10.55, -0.4) * mm, "end": v(10.55, -1.75) * mm});
            skLineSegment(sketch, "E5.10.0.5", {"start": v(10.55, 0.1) * mm, "end": v(11.05, 0.1) * mm});
            skLineSegment(sketch, "E5.10.0.6", {"start": v(10.55, 1.75) * mm, "end": v(11.05, 1.75) * mm});
            skLineSegment(sketch, "E5.10.0.7", {"start": v(10.55, -0.4) * mm, "end": v(11.05, -0.4) * mm});
            skLineSegment(sketch, "E5.10.0.8", {"start": v(10.55, -1.75) * mm, "end": v(11.05, -1.75) * mm});
            skLineSegment(sketch, "E5.11.0.0", {"start": v(11.85, -0.4) * mm, "end": v(11.85, -1.75) * mm});
            skLineSegment(sketch, "E5.11.0.1", {"start": v(11.85, 1.75) * mm, "end": v(11.85, 0.1) * mm});
            skPoint(sketch, "E5.11.0.2", {"position": v(11.6, -1.75) * mm});
            skLineSegment(sketch, "E5.11.0.3", {"start": v(11.35, 1.75) * mm, "end": v(11.35, 0.1) * mm});
            skLineSegment(sketch, "E5.11.0.4", {"start": v(11.35, -0.4) * mm, "end": v(11.35, -1.75) * mm});
            skLineSegment(sketch, "E5.11.0.5", {"start": v(11.35, 0.1) * mm, "end": v(11.85, 0.1) * mm});
            skLineSegment(sketch, "E5.11.0.6", {"start": v(11.35, 1.75) * mm, "end": v(11.85, 1.75) * mm});
            skLineSegment(sketch, "E5.11.0.7", {"start": v(11.35, -0.4) * mm, "end": v(11.85, -0.4) * mm});
            skLineSegment(sketch, "E5.11.0.8", {"start": v(11.35, -1.75) * mm, "end": v(11.85, -1.75) * mm});
            skLineSegment(sketch, "E5.12.0.0", {"start": v(12.65, -0.4) * mm, "end": v(12.65, -1.75) * mm});
            skLineSegment(sketch, "E5.12.0.1", {"start": v(12.65, 1.75) * mm, "end": v(12.65, 0.1) * mm});
            skPoint(sketch, "E5.12.0.2", {"position": v(12.4, -1.75) * mm});
            skLineSegment(sketch, "E5.12.0.3", {"start": v(12.15, 1.75) * mm, "end": v(12.15, 0.1) * mm});
            skLineSegment(sketch, "E5.12.0.4", {"start": v(12.15, -0.4) * mm, "end": v(12.15, -1.75) * mm});
            skLineSegment(sketch, "E5.12.0.5", {"start": v(12.15, 0.1) * mm, "end": v(12.65, 0.1) * mm});
            skLineSegment(sketch, "E5.12.0.6", {"start": v(12.15, 1.75) * mm, "end": v(12.65, 1.75) * mm});
            skLineSegment(sketch, "E5.12.0.7", {"start": v(12.15, -0.4) * mm, "end": v(12.65, -0.4) * mm});
            skLineSegment(sketch, "E5.12.0.8", {"start": v(12.15, -1.75) * mm, "end": v(12.65, -1.75) * mm});
            skLineSegment(sketch, "E5.13.0.0", {"start": v(13.45, -0.4) * mm, "end": v(13.45, -1.75) * mm});
            skLineSegment(sketch, "E5.13.0.1", {"start": v(13.45, 1.75) * mm, "end": v(13.45, 0.1) * mm});
            skPoint(sketch, "E5.13.0.2", {"position": v(13.2, -1.75) * mm});
            skLineSegment(sketch, "E5.13.0.3", {"start": v(12.95, 1.75) * mm, "end": v(12.95, 0.1) * mm});
            skLineSegment(sketch, "E5.13.0.4", {"start": v(12.95, -0.4) * mm, "end": v(12.95, -1.75) * mm});
            skLineSegment(sketch, "E5.13.0.5", {"start": v(12.95, 0.1) * mm, "end": v(13.45, 0.1) * mm});
            skLineSegment(sketch, "E5.13.0.6", {"start": v(12.95, 1.75) * mm, "end": v(13.45, 1.75) * mm});
            skLineSegment(sketch, "E5.13.0.7", {"start": v(12.95, -0.4) * mm, "end": v(13.45, -0.4) * mm});
            skLineSegment(sketch, "E5.13.0.8", {"start": v(12.95, -1.75) * mm, "end": v(13.45, -1.75) * mm});
            skLineSegment(sketch, "E5.14.0.0", {"start": v(14.25, -0.4) * mm, "end": v(14.25, -1.75) * mm});
            skLineSegment(sketch, "E5.14.0.1", {"start": v(14.25, 1.75) * mm, "end": v(14.25, 0.1) * mm});
            skPoint(sketch, "E5.14.0.2", {"position": v(14, -1.75) * mm});
            skLineSegment(sketch, "E5.14.0.3", {"start": v(13.75, 1.75) * mm, "end": v(13.75, 0.1) * mm});
            skLineSegment(sketch, "E5.14.0.4", {"start": v(13.75, -0.4) * mm, "end": v(13.75, -1.75) * mm});
            skLineSegment(sketch, "E5.14.0.5", {"start": v(13.75, 0.1) * mm, "end": v(14.25, 0.1) * mm});
            skLineSegment(sketch, "E5.14.0.6", {"start": v(13.75, 1.75) * mm, "end": v(14.25, 1.75) * mm});
            skLineSegment(sketch, "E5.14.0.7", {"start": v(13.75, -0.4) * mm, "end": v(14.25, -0.4) * mm});
            skLineSegment(sketch, "E5.14.0.8", {"start": v(13.75, -1.75) * mm, "end": v(14.25, -1.75) * mm});
            skLineSegment(sketch, "E5.15.0.0", {"start": v(15.05, -0.4) * mm, "end": v(15.05, -1.75) * mm});
            skLineSegment(sketch, "E5.15.0.1", {"start": v(15.05, 1.75) * mm, "end": v(15.05, 0.1) * mm});
            skPoint(sketch, "E5.15.0.2", {"position": v(14.8, -1.75) * mm});
            skLineSegment(sketch, "E5.15.0.3", {"start": v(14.55, 1.75) * mm, "end": v(14.55, 0.1) * mm});
            skLineSegment(sketch, "E5.15.0.4", {"start": v(14.55, -0.4) * mm, "end": v(14.55, -1.75) * mm});
            skLineSegment(sketch, "E5.15.0.5", {"start": v(14.55, 0.1) * mm, "end": v(15.05, 0.1) * mm});
            skLineSegment(sketch, "E5.15.0.6", {"start": v(14.55, 1.75) * mm, "end": v(15.05, 1.75) * mm});
            skLineSegment(sketch, "E5.15.0.7", {"start": v(14.55, -0.4) * mm, "end": v(15.05, -0.4) * mm});
            skLineSegment(sketch, "E5.15.0.8", {"start": v(14.55, -1.75) * mm, "end": v(15.05, -1.75) * mm});
            skLineSegment(sketch, "E5.16.0.0", {"start": v(15.85, -0.4) * mm, "end": v(15.85, -1.75) * mm});
            skLineSegment(sketch, "E5.16.0.1", {"start": v(15.85, 1.75) * mm, "end": v(15.85, 0.1) * mm});
            skPoint(sketch, "E5.16.0.2", {"position": v(15.6, -1.75) * mm});
            skLineSegment(sketch, "E5.16.0.3", {"start": v(15.35, 1.75) * mm, "end": v(15.35, 0.1) * mm});
            skLineSegment(sketch, "E5.16.0.4", {"start": v(15.35, -0.4) * mm, "end": v(15.35, -1.75) * mm});
            skLineSegment(sketch, "E5.16.0.5", {"start": v(15.35, 0.1) * mm, "end": v(15.85, 0.1) * mm});
            skLineSegment(sketch, "E5.16.0.6", {"start": v(15.35, 1.75) * mm, "end": v(15.85, 1.75) * mm});
            skLineSegment(sketch, "E5.16.0.7", {"start": v(15.35, -0.4) * mm, "end": v(15.85, -0.4) * mm});
            skLineSegment(sketch, "E5.16.0.8", {"start": v(15.35, -1.75) * mm, "end": v(15.85, -1.75) * mm});
            skLineSegment(sketch, "E5.17.0.0", {"start": v(16.65, -0.4) * mm, "end": v(16.65, -1.75) * mm});
            skLineSegment(sketch, "E5.17.0.1", {"start": v(16.65, 1.75) * mm, "end": v(16.65, 0.1) * mm});
            skPoint(sketch, "E5.17.0.2", {"position": v(16.4, -1.75) * mm});
            skLineSegment(sketch, "E5.17.0.3", {"start": v(16.15, 1.75) * mm, "end": v(16.15, 0.1) * mm});
            skLineSegment(sketch, "E5.17.0.4", {"start": v(16.15, -0.4) * mm, "end": v(16.15, -1.75) * mm});
            skLineSegment(sketch, "E5.17.0.5", {"start": v(16.15, 0.1) * mm, "end": v(16.65, 0.1) * mm});
            skLineSegment(sketch, "E5.17.0.6", {"start": v(16.15, 1.75) * mm, "end": v(16.65, 1.75) * mm});
            skLineSegment(sketch, "E5.17.0.7", {"start": v(16.15, -0.4) * mm, "end": v(16.65, -0.4) * mm});
            skLineSegment(sketch, "E5.17.0.8", {"start": v(16.15, -1.75) * mm, "end": v(16.65, -1.75) * mm});
            skLineSegment(sketch, "E5.18.0.0", {"start": v(17.45, -0.4) * mm, "end": v(17.45, -1.75) * mm});
            skLineSegment(sketch, "E5.18.0.1", {"start": v(17.45, 1.75) * mm, "end": v(17.45, 0.1) * mm});
            skPoint(sketch, "E5.18.0.2", {"position": v(17.2, -1.75) * mm});
            skLineSegment(sketch, "E5.18.0.3", {"start": v(16.95, 1.75) * mm, "end": v(16.95, 0.1) * mm});
            skLineSegment(sketch, "E5.18.0.4", {"start": v(16.95, -0.4) * mm, "end": v(16.95, -1.75) * mm});
            skLineSegment(sketch, "E5.18.0.5", {"start": v(16.95, 0.1) * mm, "end": v(17.45, 0.1) * mm});
            skLineSegment(sketch, "E5.18.0.6", {"start": v(16.95, 1.75) * mm, "end": v(17.45, 1.75) * mm});
            skLineSegment(sketch, "E5.18.0.7", {"start": v(16.95, -0.4) * mm, "end": v(17.45, -0.4) * mm});
            skLineSegment(sketch, "E5.18.0.8", {"start": v(16.95, -1.75) * mm, "end": v(17.45, -1.75) * mm});
            skLineSegment(sketch, "E5.19.0.0", {"start": v(18.25, -0.4) * mm, "end": v(18.25, -1.75) * mm});
            skLineSegment(sketch, "E5.19.0.1", {"start": v(18.25, 1.75) * mm, "end": v(18.25, 0.1) * mm});
            skPoint(sketch, "E5.19.0.2", {"position": v(18, -1.75) * mm});
            skLineSegment(sketch, "E5.19.0.3", {"start": v(17.75, 1.75) * mm, "end": v(17.75, 0.1) * mm});
            skLineSegment(sketch, "E5.19.0.4", {"start": v(17.75, -0.4) * mm, "end": v(17.75, -1.75) * mm});
            skLineSegment(sketch, "E5.19.0.5", {"start": v(17.75, 0.1) * mm, "end": v(18.25, 0.1) * mm});
            skLineSegment(sketch, "E5.19.0.6", {"start": v(17.75, 1.75) * mm, "end": v(18.25, 1.75) * mm});
            skLineSegment(sketch, "E5.19.0.7", {"start": v(17.75, -0.4) * mm, "end": v(18.25, -0.4) * mm});
            skLineSegment(sketch, "E5.19.0.8", {"start": v(17.75, -1.75) * mm, "end": v(18.25, -1.75) * mm});
            skLineSegment(sketch, "E5.20.0.0", {"start": v(19.05, -0.4) * mm, "end": v(19.05, -1.75) * mm});
            skLineSegment(sketch, "E5.20.0.1", {"start": v(19.05, 1.75) * mm, "end": v(19.05, 0.1) * mm});
            skPoint(sketch, "E5.20.0.2", {"position": v(18.8, -1.75) * mm});
            skLineSegment(sketch, "E5.20.0.3", {"start": v(18.55, 1.75) * mm, "end": v(18.55, 0.1) * mm});
            skLineSegment(sketch, "E5.20.0.4", {"start": v(18.55, -0.4) * mm, "end": v(18.55, -1.75) * mm});
            skLineSegment(sketch, "E5.20.0.5", {"start": v(18.55, 0.1) * mm, "end": v(19.05, 0.1) * mm});
            skLineSegment(sketch, "E5.20.0.6", {"start": v(18.55, 1.75) * mm, "end": v(19.05, 1.75) * mm});
            skLineSegment(sketch, "E5.20.0.7", {"start": v(18.55, -0.4) * mm, "end": v(19.05, -0.4) * mm});
            skLineSegment(sketch, "E5.20.0.8", {"start": v(18.55, -1.75) * mm, "end": v(19.05, -1.75) * mm});
            skLineSegment(sketch, "E5.21.0.0", {"start": v(19.85, -0.4) * mm, "end": v(19.85, -1.75) * mm});
            skLineSegment(sketch, "E5.21.0.1", {"start": v(19.85, 1.75) * mm, "end": v(19.85, 0.1) * mm});
            skPoint(sketch, "E5.21.0.2", {"position": v(19.6, -1.75) * mm});
            skLineSegment(sketch, "E5.21.0.3", {"start": v(19.35, 1.75) * mm, "end": v(19.35, 0.1) * mm});
            skLineSegment(sketch, "E5.21.0.4", {"start": v(19.35, -0.4) * mm, "end": v(19.35, -1.75) * mm});
            skLineSegment(sketch, "E5.21.0.5", {"start": v(19.35, 0.1) * mm, "end": v(19.85, 0.1) * mm});
            skLineSegment(sketch, "E5.21.0.6", {"start": v(19.35, 1.75) * mm, "end": v(19.85, 1.75) * mm});
            skLineSegment(sketch, "E5.21.0.7", {"start": v(19.35, -0.4) * mm, "end": v(19.85, -0.4) * mm});
            skLineSegment(sketch, "E5.21.0.8", {"start": v(19.35, -1.75) * mm, "end": v(19.85, -1.75) * mm});
            skLineSegment(sketch, "E5.22.0.0", {"start": v(20.65, -0.4) * mm, "end": v(20.65, -1.75) * mm});
            skLineSegment(sketch, "E5.22.0.1", {"start": v(20.65, 1.75) * mm, "end": v(20.65, 0.1) * mm});
            skPoint(sketch, "E5.22.0.2", {"position": v(20.4, -1.75) * mm});
            skLineSegment(sketch, "E5.22.0.3", {"start": v(20.15, 1.75) * mm, "end": v(20.15, 0.1) * mm});
            skLineSegment(sketch, "E5.22.0.4", {"start": v(20.15, -0.4) * mm, "end": v(20.15, -1.75) * mm});
            skLineSegment(sketch, "E5.22.0.5", {"start": v(20.15, 0.1) * mm, "end": v(20.65, 0.1) * mm});
            skLineSegment(sketch, "E5.22.0.6", {"start": v(20.15, 1.75) * mm, "end": v(20.65, 1.75) * mm});
            skLineSegment(sketch, "E5.22.0.7", {"start": v(20.15, -0.4) * mm, "end": v(20.65, -0.4) * mm});
            skLineSegment(sketch, "E5.22.0.8", {"start": v(20.15, -1.75) * mm, "end": v(20.65, -1.75) * mm});
            skLineSegment(sketch, "E5.23.0.0", {"start": v(21.45, -0.4) * mm, "end": v(21.45, -1.75) * mm});
            skLineSegment(sketch, "E5.23.0.1", {"start": v(21.45, 1.75) * mm, "end": v(21.45, 0.1) * mm});
            skPoint(sketch, "E5.23.0.2", {"position": v(21.2, -1.75) * mm});
            skLineSegment(sketch, "E5.23.0.3", {"start": v(20.95, 1.75) * mm, "end": v(20.95, 0.1) * mm});
            skLineSegment(sketch, "E5.23.0.4", {"start": v(20.95, -0.4) * mm, "end": v(20.95, -1.75) * mm});
            skLineSegment(sketch, "E5.23.0.5", {"start": v(20.95, 0.1) * mm, "end": v(21.45, 0.1) * mm});
            skLineSegment(sketch, "E5.23.0.6", {"start": v(20.95, 1.75) * mm, "end": v(21.45, 1.75) * mm});
            skLineSegment(sketch, "E5.23.0.7", {"start": v(20.95, -0.4) * mm, "end": v(21.45, -0.4) * mm});
            skLineSegment(sketch, "E5.23.0.8", {"start": v(20.95, -1.75) * mm, "end": v(21.45, -1.75) * mm});
            skLineSegment(sketch, "E5.24.0.0", {"start": v(22.25, -0.4) * mm, "end": v(22.25, -1.75) * mm});
            skLineSegment(sketch, "E5.24.0.1", {"start": v(22.25, 1.75) * mm, "end": v(22.25, 0.1) * mm});
            skPoint(sketch, "E5.24.0.2", {"position": v(22, -1.75) * mm});
            skLineSegment(sketch, "E5.24.0.3", {"start": v(21.75, 1.75) * mm, "end": v(21.75, 0.1) * mm});
            skLineSegment(sketch, "E5.24.0.4", {"start": v(21.75, -0.4) * mm, "end": v(21.75, -1.75) * mm});
            skLineSegment(sketch, "E5.24.0.5", {"start": v(21.75, 0.1) * mm, "end": v(22.25, 0.1) * mm});
            skLineSegment(sketch, "E5.24.0.6", {"start": v(21.75, 1.75) * mm, "end": v(22.25, 1.75) * mm});
            skLineSegment(sketch, "E5.24.0.7", {"start": v(21.75, -0.4) * mm, "end": v(22.25, -0.4) * mm});
            skLineSegment(sketch, "E5.24.0.8", {"start": v(21.75, -1.75) * mm, "end": v(22.25, -1.75) * mm});
            skLineSegment(sketch, "E5.25.0.0", {"start": v(23.05, -0.4) * mm, "end": v(23.05, -1.75) * mm});
            skLineSegment(sketch, "E5.25.0.1", {"start": v(23.05, 1.75) * mm, "end": v(23.05, 0.1) * mm});
            skPoint(sketch, "E5.25.0.2", {"position": v(22.8, -1.75) * mm});
            skLineSegment(sketch, "E5.25.0.3", {"start": v(22.55, 1.75) * mm, "end": v(22.55, 0.1) * mm});
            skLineSegment(sketch, "E5.25.0.4", {"start": v(22.55, -0.4) * mm, "end": v(22.55, -1.75) * mm});
            skLineSegment(sketch, "E5.25.0.5", {"start": v(22.55, 0.1) * mm, "end": v(23.05, 0.1) * mm});
            skLineSegment(sketch, "E5.25.0.6", {"start": v(22.55, 1.75) * mm, "end": v(23.05, 1.75) * mm});
            skLineSegment(sketch, "E5.25.0.7", {"start": v(22.55, -0.4) * mm, "end": v(23.05, -0.4) * mm});
            skLineSegment(sketch, "E5.25.0.8", {"start": v(22.55, -1.75) * mm, "end": v(23.05, -1.75) * mm});
            skLineSegment(sketch, "E5.26.0.0", {"start": v(23.85, -0.4) * mm, "end": v(23.85, -1.75) * mm});
            skLineSegment(sketch, "E5.26.0.1", {"start": v(23.85, 1.75) * mm, "end": v(23.85, 0.1) * mm});
            skPoint(sketch, "E5.26.0.2", {"position": v(23.6, -1.75) * mm});
            skLineSegment(sketch, "E5.26.0.3", {"start": v(23.35, 1.75) * mm, "end": v(23.35, 0.1) * mm});
            skLineSegment(sketch, "E5.26.0.4", {"start": v(23.35, -0.4) * mm, "end": v(23.35, -1.75) * mm});
            skLineSegment(sketch, "E5.26.0.5", {"start": v(23.35, 0.1) * mm, "end": v(23.85, 0.1) * mm});
            skLineSegment(sketch, "E5.26.0.6", {"start": v(23.35, 1.75) * mm, "end": v(23.85, 1.75) * mm});
            skLineSegment(sketch, "E5.26.0.7", {"start": v(23.35, -0.4) * mm, "end": v(23.85, -0.4) * mm});
            skLineSegment(sketch, "E5.26.0.8", {"start": v(23.35, -1.75) * mm, "end": v(23.85, -1.75) * mm});
            skLineSegment(sketch, "E5.27.0.0", {"start": v(24.65, -0.4) * mm, "end": v(24.65, -1.75) * mm});
            skLineSegment(sketch, "E5.27.0.1", {"start": v(24.65, 1.75) * mm, "end": v(24.65, 0.1) * mm});
            skPoint(sketch, "E5.27.0.2", {"position": v(24.4, -1.75) * mm});
            skLineSegment(sketch, "E5.27.0.3", {"start": v(24.15, 1.75) * mm, "end": v(24.15, 0.1) * mm});
            skLineSegment(sketch, "E5.27.0.4", {"start": v(24.15, -0.4) * mm, "end": v(24.15, -1.75) * mm});
            skLineSegment(sketch, "E5.27.0.5", {"start": v(24.15, 0.1) * mm, "end": v(24.65, 0.1) * mm});
            skLineSegment(sketch, "E5.27.0.6", {"start": v(24.15, 1.75) * mm, "end": v(24.65, 1.75) * mm});
            skLineSegment(sketch, "E5.27.0.7", {"start": v(24.15, -0.4) * mm, "end": v(24.65, -0.4) * mm});
            skLineSegment(sketch, "E5.27.0.8", {"start": v(24.15, -1.75) * mm, "end": v(24.65, -1.75) * mm});
            skLineSegment(sketch, "E5.direction1", {"start": v(2.55, -1.75) * mm, "end": v(3.35, -1.75) * mm, "construction": true});
            skLineSegment(sketch, "E6.0.2.0", {"start": v(6.55, 0.1) * mm, "end": v(7.05, 0.1) * mm, "construction": true});
            skLineSegment(sketch, "E6.3.2.0", {"start": v(7.05, -0.4) * mm, "end": v(7.05, -1.75) * mm, "construction": true});
            skLineSegment(sketch, "E6.6.2.0", {"start": v(6.55, 1.75) * mm, "end": v(6.55, 0.1) * mm, "construction": true});
            skLineSegment(sketch, "E6.9.2.0", {"start": v(7.05, 1.75) * mm, "end": v(7.05, 0.1) * mm, "construction": true});
            skLineSegment(sketch, "E6.12.2.0", {"start": v(6.55, -0.4) * mm, "end": v(7.05, -0.4) * mm, "construction": true});
            skLineSegment(sketch, "E6.16.2.0", {"start": v(6.55, -0.4) * mm, "end": v(6.55, -1.75) * mm, "construction": true});
            skLineSegment(sketch, "E6.19.2.0", {"start": v(6.55, 1.75) * mm, "end": v(7.05, 1.75) * mm, "construction": true});
            skLineSegment(sketch, "E6.22.2.0", {"start": v(6.55, -1.75) * mm, "end": v(7.05, -1.75) * mm, "construction": true});
            skPoint(sketch, "E7", {"position": v(25.2, 0.93) * mm});
            skPoint(sketch, "E7.positionSnap0", {"position": v(25.2, 0.1) * mm});
            skPoint(sketch, "E7.positionSnap1", {"position": v(25.45, 0.93) * mm});
            skPoint(sketch, "E8", {"position": v(25.2, -1.07) * mm});
            skPoint(sketch, "E8.positionSnap0", {"position": v(25.45, -1.07) * mm});
            skLineSegment(sketch, "E9.0.28.0", {"start": v(25.45, -0.4) * mm, "end": v(25.45, -1.75) * mm, "construction": true});
            skLineSegment(sketch, "E9.3.28.0", {"start": v(25.45, 1.75) * mm, "end": v(25.45, 0.1) * mm, "construction": true});
            skPoint(sketch, "E9.6.28.0", {"position": v(25.2, -1.75) * mm});
            skLineSegment(sketch, "E9.7.28.0", {"start": v(24.95, 1.75) * mm, "end": v(24.95, 0.1) * mm, "construction": true});
            skLineSegment(sketch, "E9.10.28.0", {"start": v(24.95, -0.4) * mm, "end": v(24.95, -1.75) * mm, "construction": true});
            skLineSegment(sketch, "E9.13.28.0", {"start": v(24.95, 0.1) * mm, "end": v(25.45, 0.1) * mm, "construction": true});
            skLineSegment(sketch, "E9.16.28.0", {"start": v(24.95, 1.75) * mm, "end": v(25.45, 1.75) * mm, "construction": true});
            skLineSegment(sketch, "E9.19.28.0", {"start": v(24.95, -0.4) * mm, "end": v(25.45, -0.4) * mm, "construction": true});
            skLineSegment(sketch, "E9.22.28.0", {"start": v(24.95, -1.75) * mm, "end": v(25.45, -1.75) * mm, "construction": true});
            skLineSegment(sketch, "E10.0.31.0", {"start": v(-0.15, 1.75) * mm, "end": v(-0.15, 0.1) * mm});
            skLineSegment(sketch, "E10.3.31.0", {"start": v(-0.65, -0.4) * mm, "end": v(-0.65, -1.75) * mm});
            skLineSegment(sketch, "E10.6.31.0", {"start": v(-0.65, 0.1) * mm, "end": v(-0.15, 0.1) * mm});
            skLineSegment(sketch, "E10.9.31.0", {"start": v(-0.15, -0.4) * mm, "end": v(-0.15, -1.75) * mm});
            skPoint(sketch, "E10.12.31.0", {"position": v(-0.4, -1.75) * mm});
            skLineSegment(sketch, "E10.13.31.0", {"start": v(-0.65, -0.4) * mm, "end": v(-0.15, -0.4) * mm});
            skLineSegment(sketch, "E10.16.31.0", {"start": v(-0.65, 1.75) * mm, "end": v(-0.15, 1.75) * mm});
            skLineSegment(sketch, "E10.19.31.0", {"start": v(-0.65, 1.75) * mm, "end": v(-0.65, 0.1) * mm});
            skLineSegment(sketch, "E10.22.31.0", {"start": v(-0.65, -1.75) * mm, "end": v(-0.15, -1.75) * mm});
            skCircle(sketch, "E11", {"center": v(28.3, 0) * mm, "radius": 0.7 * mm});
            skCircle(sketch, "E12", {"center": v(27.35, 7) * mm, "radius": 0.4 * mm});
            skLineSegment(sketch, "E13", {"start": v(0, 0) * mm, "end": v(-0.15, -18.58) * mm, "construction": true});
            skPoint(sketch, "E13.endSnap0", {"position": v(-0.15, 0.93) * mm});
            skCircle(sketch, "E14.MirrorC", {"center": v(-28.3, 0.46) * mm, "radius": 0.7 * mm});
            skCircle(sketch, "E15.MirrorC", {"center": v(-27.23, 7.44) * mm, "radius": 0.4 * mm});
            skSolve(sketch);
        }
        {
            var Q0;
            Q0 = qSketchRegion(id + "F0", true);
            extrude(context, id + "F1", {"entities" : qUnion([Q0]), "depth" : 0.1 * mm, "offsetDistance" : 25 * mm});
        }
    });
